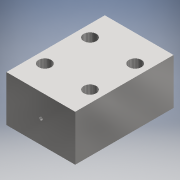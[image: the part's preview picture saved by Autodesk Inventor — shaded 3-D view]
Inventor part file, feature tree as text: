
AUTODESK INVENTOR PART (.ipt)
format: ipt  version: 2016 (Build 200138000, 138)  size: 159,232 bytes
history: native  units: mm (DEFAULTED — no unit token found)
features: extrude x5, sketch x5, hole x2, mirror x1, other x1, fillet x1
ambient origin geometry x8: Origin, YZ Plane, XZ Plane, XY Plane, X Axis, Y Axis, Z Axis, Center Point
bodies: Solid1 (feature_tree)
feature tree (15):
  extrude  "Stock Block"  Depth=76.2mm
  hole  "Spring Hole"  [1 undecoded]
  extrude  "Mounting Holes"  Depth=14.0mm
  hole  "Mounting Holes Secondary"  [1 undecoded]
  mirror  "Mirror2"
  other  "Insert Sketch"
  extrude  "Insert Depression"  Depth=4.0mm
  extrude  "Insert Slot"  Depth=4.0mm
  extrude  "Insert Holes"  Depth=4.0mm TaperAngle=0.0deg
  fillet  "Insert Slot Fillet"  Radius=6.604mm
  sketch  "Sketch2"  dims[d0=109.0mm d1=76.2mm]
  sketch  "Sketch3"  dims[d2=50.8mm d3=0.0mm]
  sketch  "Sketch4"  dims[d4=4.134mm d5=10.0mm d6=4.0mm d7=2.0mm d8=90.0deg d9=12.7mm d10=20.594885mm d11=50.0mm]
  sketch  "Sketch5"  dims[d12=50.0mm d14=14.0mm]
  sketch  "Sketch9"  dims[d17=30.48mm d18=0.0mm d19=8.0mm d20=6.0mm d21=4.0mm d22=2.0mm d23=90.0deg d24=8.0mm d25=20.594885mm d31=3.5mm d32=6.35mm d33=25.4mm d34=22.0mm d35=0.0mm d36=6.604mm d38=19.05mm d39=38.1mm d40=0.0mm d41=3.5mm d42=7.9375mm d43=6.0mm d44=6.0mm d45=3.0mm d46=0.0mm d47=3.175mm]
note: 2 required parameter values undecoded (feature->parameter linkage not recoverable at this tier; creation-order binding heuristic only, values carry confidence <= 0.55)
